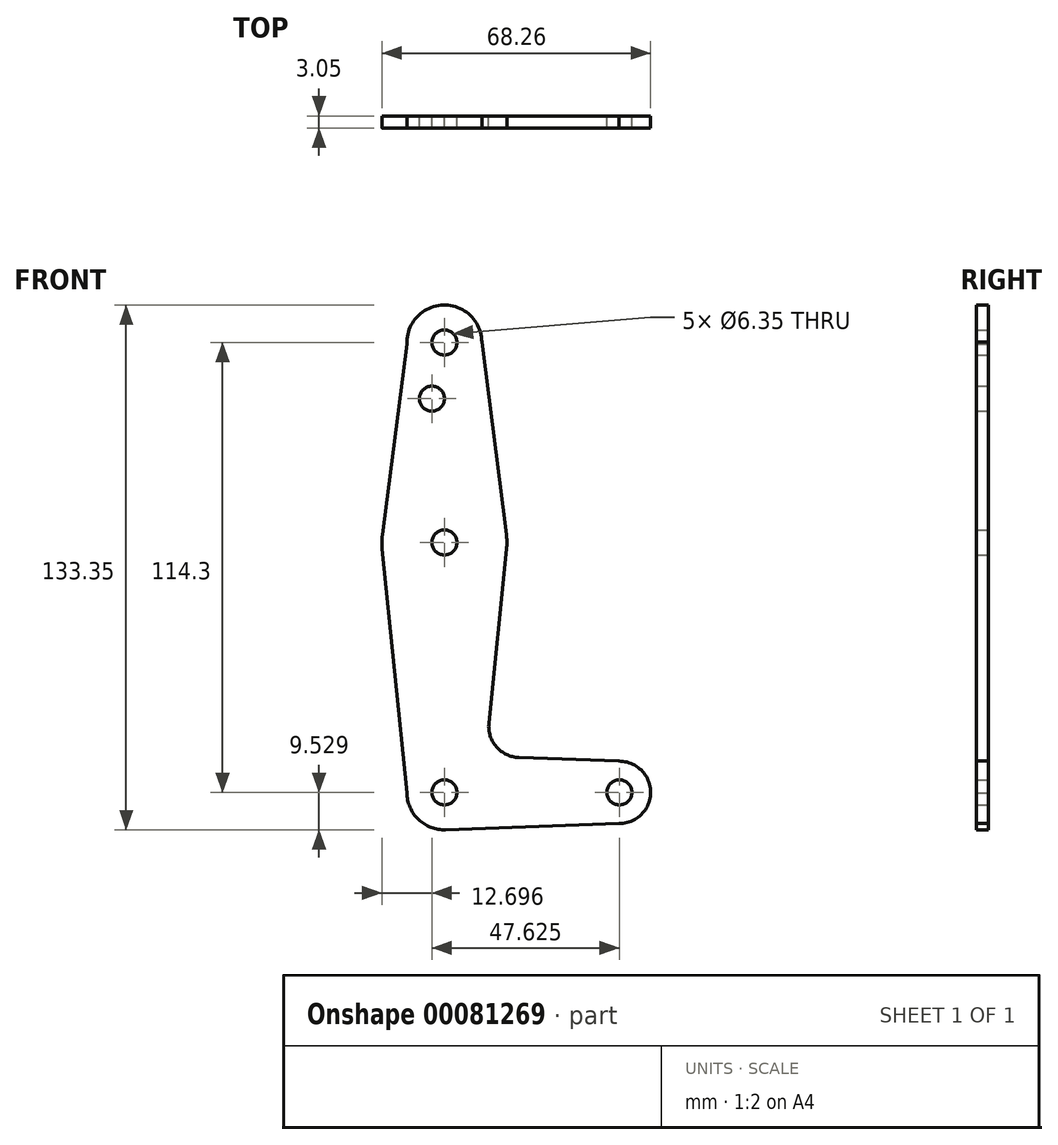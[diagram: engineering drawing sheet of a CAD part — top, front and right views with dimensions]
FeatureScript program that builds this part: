
annotation { "Feature Type Name" : "Feature", "Feature Type Description" : "" }
export const myFeature = defineFeature(function(context is Context, id is Id, definition is map)
    precondition{}
    {
        {
            var Q0;
            Q0=qCreatedBy(makeId("Front.planeOp"),FACE);
            var sketch = newSketch(context, id + "F0", { "sketchPlane" : qUnion([Q0])});
            skCircle(sketch, "E0", {"center": v(-60.88, 80.69) * mm, "radius": 9.53 * mm});
            skCircle(sketch, "E1", {"center": v(-16.43, -33.61) * mm, "radius": 7.94 * mm});
            skCircle(sketch, "E2", {"center": v(-60.88, 29.89) * mm, "radius": 15.88 * mm});
            skCircle(sketch, "E3", {"center": v(-60.88, -33.61) * mm, "radius": 9.53 * mm});
            skLineSegment(sketch, "E4", {"start": v(-16.53, -41.55) * mm, "end": v(-60.54, -43.13) * mm});
            skLineSegment(sketch, "E5", {"start": v(-15.74, -25.7) * mm, "end": v(-41.95, -24.76) * mm});
            skLineSegment(sketch, "E6", {"start": v(-49.57, -16.01) * mm, "end": v(-45.08, 28.29) * mm});
            skLineSegment(sketch, "E7", {"start": v(-70.4, -33.7) * mm, "end": v(-76.67, 28.3) * mm});
            skLineSegment(sketch, "E8", {"start": v(-70.4, 80.26) * mm, "end": v(-76.62, 31.92) * mm});
            skLineSegment(sketch, "E9", {"start": v(-51.35, 80.84) * mm, "end": v(-45.13, 31.9) * mm});
            skCircle(sketch, "E10", {"center": v(-60.88, 80.69) * mm, "radius": 3.18 * mm});
            skCircle(sketch, "E11", {"center": v(-60.88, 29.89) * mm, "radius": 3.18 * mm});
            skCircle(sketch, "E12", {"center": v(-60.88, -33.61) * mm, "radius": 3.18 * mm});
            skCircle(sketch, "E13", {"center": v(-16.43, -33.61) * mm, "radius": 3.18 * mm});
            skCircle(sketch, "E14", {"center": v(-64.05, 66.41) * mm, "radius": 3.18 * mm});
            skArc(sketch, "E15.filletArc", {"start": v(-49.57, -16.01) * mm, "mid": v(-47.65, -22.04) * mm, "end": v(-41.95, -24.76) * mm});
            skSolve(sketch);
        }
        {
            var Q0;
            Q0 = qSketchRegion(id + "F0", true);
            extrude(context, id + "F1", {"entities" : qUnion([Q0]), "depth" : 3.05 * mm});
        }
    });
